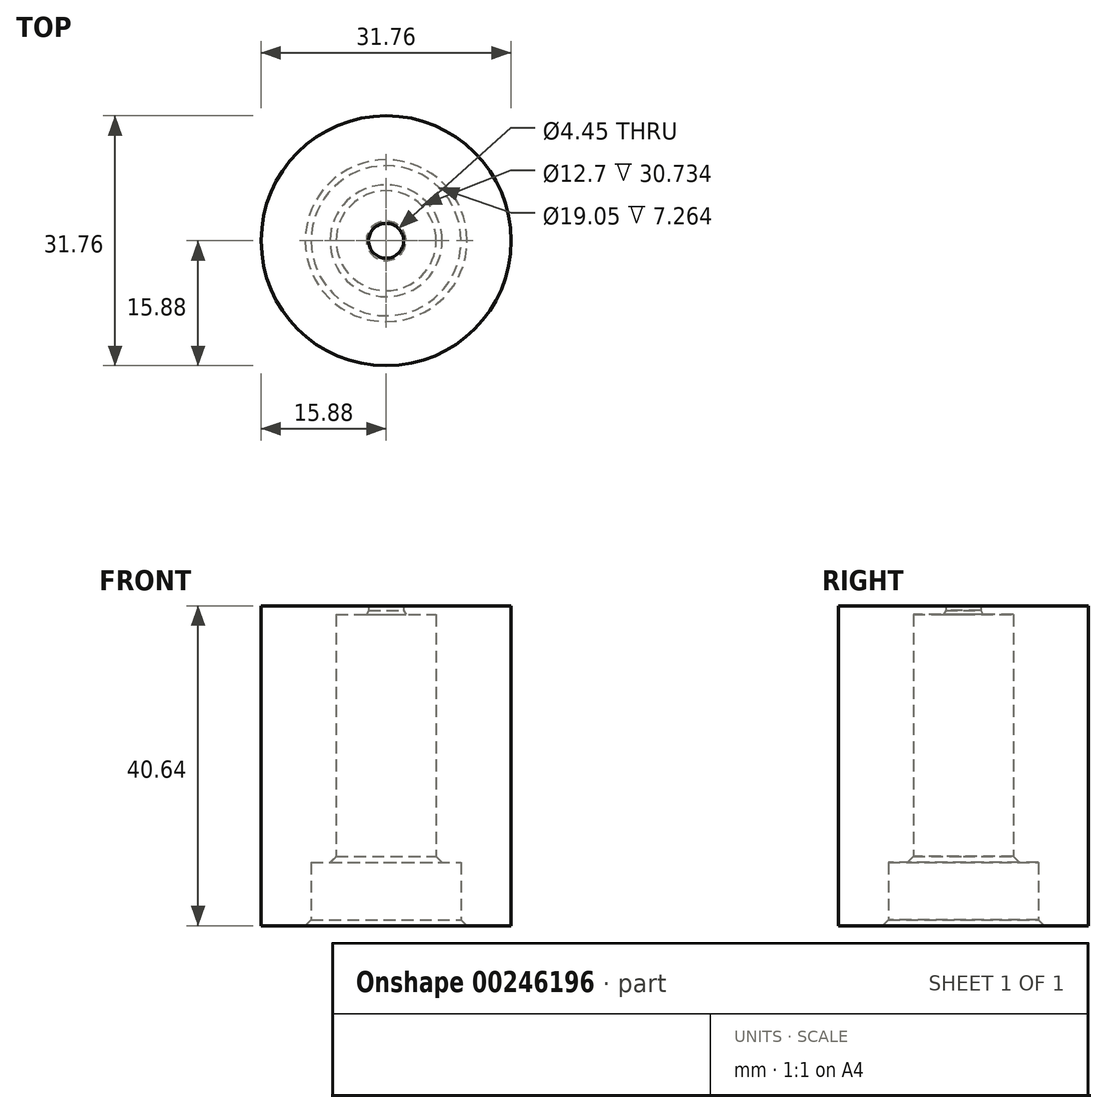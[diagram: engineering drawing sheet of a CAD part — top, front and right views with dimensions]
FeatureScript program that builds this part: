
annotation { "Feature Type Name" : "Feature", "Feature Type Description" : "" }
export const myFeature = defineFeature(function(context is Context, id is Id, definition is map)
    precondition{}
    {
        {
            var Q0;
            Q0=qCreatedBy(makeId("Right.planeOp"),FACE);
            var sketch = newSketch(context, id + "F0", { "sketchPlane" : qUnion([Q0])});
            skLineSegment(sketch, "E0", {"start": v(0, 0) * mm, "end": v(0, 40.64) * mm});
            skLineSegment(sketch, "E1", {"start": v(2.22, 40.64) * mm, "end": v(2.22, 39.52) * mm});
            skLineSegment(sketch, "E2", {"start": v(2.22, 39.52) * mm, "end": v(6.35, 39.52) * mm});
            skLineSegment(sketch, "E3", {"start": v(6.35, 39.52) * mm, "end": v(6.35, 8.03) * mm});
            skLineSegment(sketch, "E4", {"start": v(6.35, 8.03) * mm, "end": v(9.53, 8.03) * mm});
            skLineSegment(sketch, "E5", {"start": v(9.53, 8.03) * mm, "end": v(9.53, 0) * mm});
            skLineSegment(sketch, "E6", {"start": v(9.53, 0) * mm, "end": v(15.88, 0) * mm});
            skLineSegment(sketch, "E7", {"start": v(15.88, 0) * mm, "end": v(15.88, 40.64) * mm});
            skLineSegment(sketch, "E8", {"start": v(15.88, 40.64) * mm, "end": v(2.22, 40.64) * mm});
            skSolve(sketch);
        }
        {
            var Q0;
            Q0=makeQuery(id+"F0.imprint","IMPRINT",FACE,{"disambiguationData":[TD([[makeQuery(id+"F0.imprint","IMPRINT",EDGE,{"derivedFrom":sQuery(id+"F0.wireOp",EDGE,"E1")}),1.0]])]});
            var Q1;
            Q1=sQuery(id+"F0.wireOp",EDGE,"E0");
            revolve(context, id + "F1", {"entities" : qUnion([Q0]), "axis" : qUnion([Q1]), "revolveType" : RevolveType.FULL});
        }
        {
            var Q0;
            Q0=makeQuery(id+"F1.opRevolve","SWEPT_EDGE",EDGE,{"disambiguationData":[OSD([sQuery(id+"F0.wireOp",EDGE,"E1"),sQuery(id+"F0.wireOp",EDGE,"E2")])]});
            chamfer(context, id + "F2", {"entities" : qUnion([Q0]), "chamferType" : ChamferType.OFFSET_ANGLE, "width" : 0.5 * mm, "oppositeDirection" : false, "angle" : 30 * degree, "tangentPropagation" : true});
        }
        {
            var Q0;
            Q0=makeQuery(id+"F1.opRevolve","SWEPT_EDGE",EDGE,{"disambiguationData":[OSD([sQuery(id+"F0.wireOp",EDGE,"E3"),sQuery(id+"F0.wireOp",EDGE,"E4")])]});
            var Q1;
            Q1=makeQuery(id+"F1.opRevolve","SWEPT_EDGE",EDGE,{"disambiguationData":[OSD([sQuery(id+"F0.wireOp",EDGE,"E5"),sQuery(id+"F0.wireOp",EDGE,"E6")])]});
            chamfer(context, id + "F3", {"entities" : qUnion([Q0, Q1]), "width" : 0.76 * mm, "tangentPropagation" : true});
        }
    });
